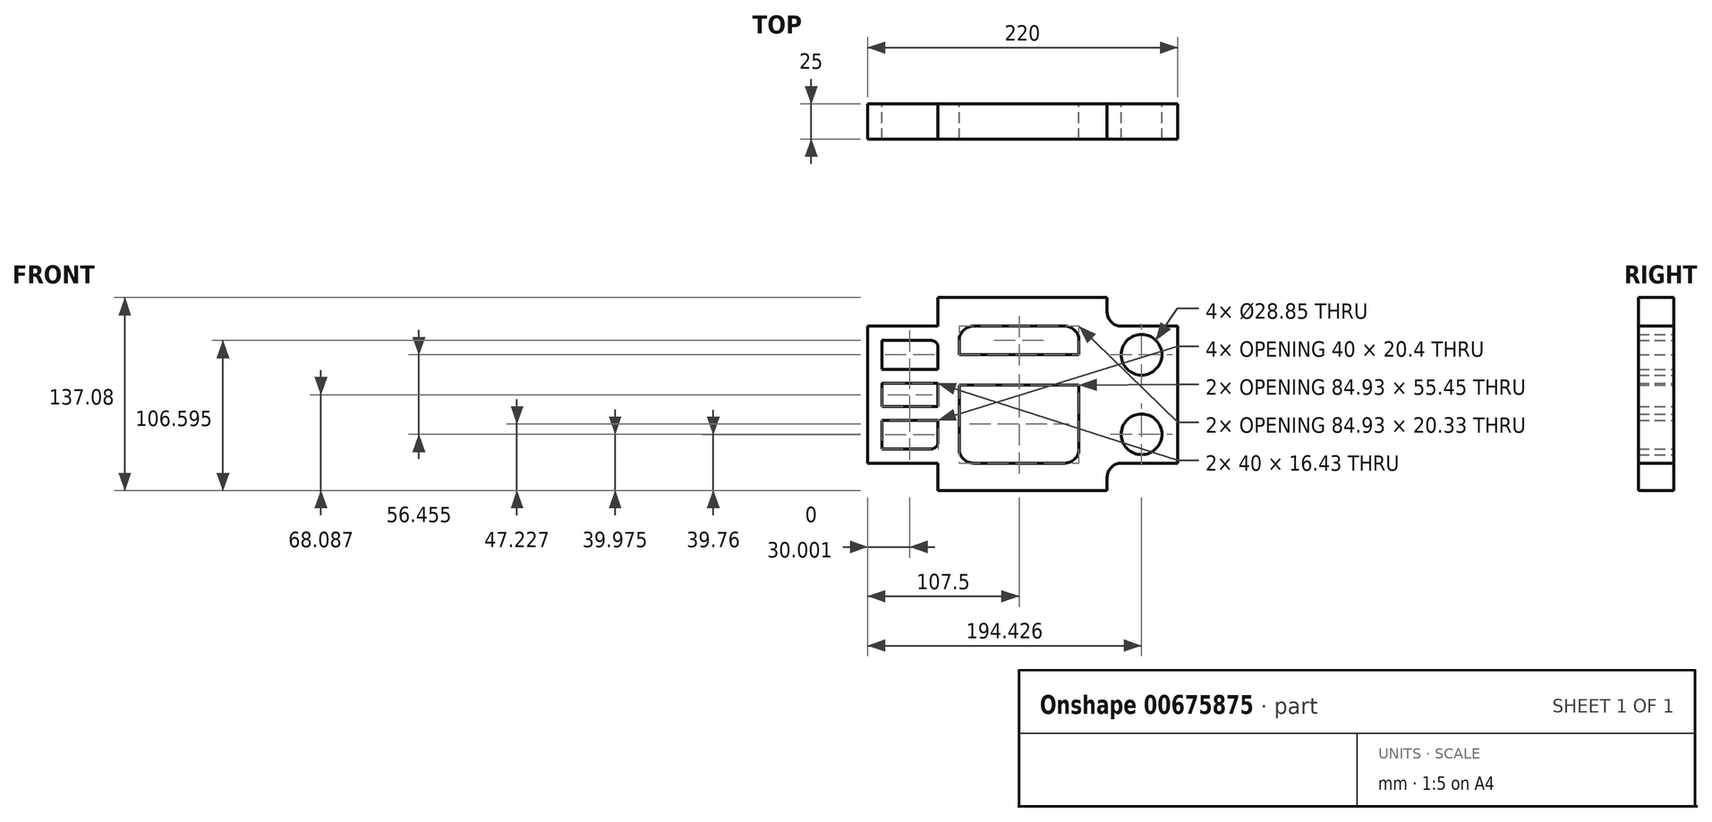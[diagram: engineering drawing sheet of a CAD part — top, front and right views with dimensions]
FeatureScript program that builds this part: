
annotation { "Feature Type Name" : "Feature", "Feature Type Description" : "" }
export const myFeature = defineFeature(function(context is Context, id is Id, definition is map)
    precondition{}
    {
        {
            var Q0;
            Q0=qCreatedBy(makeId("Front.planeOp"),FACE);
            var sketch = newSketch(context, id + "F0", { "sketchPlane" : qUnion([Q0])});
            skLineSegment(sketch, "E0", {"start": v(-52.53, 54.48) * mm, "end": v(-52.53, -42.78) * mm});
            skLineSegment(sketch, "E1", {"start": v(-52.53, -42.78) * mm, "end": v(-2.53, -42.78) * mm});
            skLineSegment(sketch, "E2", {"start": v(-2.53, -42.78) * mm, "end": v(-2.53, -62.28) * mm});
            skLineSegment(sketch, "E3", {"start": v(-2.53, -62.28) * mm, "end": v(117.47, -62.28) * mm});
            skLineSegment(sketch, "E4", {"start": v(117.47, -62.28) * mm, "end": v(117.47, -52.78) * mm});
            skLineSegment(sketch, "E5", {"start": v(127.47, -42.78) * mm, "end": v(167.47, -42.78) * mm});
            skLineSegment(sketch, "E6", {"start": v(167.47, -42.78) * mm, "end": v(167.47, 54.48) * mm});
            skLineSegment(sketch, "E7", {"start": v(167.47, 54.48) * mm, "end": v(127.47, 54.48) * mm});
            skLineSegment(sketch, "E8", {"start": v(117.47, 64.48) * mm, "end": v(117.47, 74.8) * mm});
            skLineSegment(sketch, "E9", {"start": v(117.47, 74.8) * mm, "end": v(-2.53, 74.8) * mm});
            skLineSegment(sketch, "E10", {"start": v(-2.53, 74.8) * mm, "end": v(-2.53, 54.48) * mm});
            skLineSegment(sketch, "E11", {"start": v(-2.53, 54.48) * mm, "end": v(-52.53, 54.48) * mm});
            skLineSegment(sketch, "E12", {"start": v(-2.53, 39.33) * mm, "end": v(-2.53, 23.94) * mm});
            skLineSegment(sketch, "E13", {"start": v(-42.53, -32.72) * mm, "end": v(-42.53, -12.32) * mm});
            skLineSegment(sketch, "E14", {"start": v(-42.53, -32.72) * mm, "end": v(-7.53, -32.72) * mm});
            skLineSegment(sketch, "E15", {"start": v(-42.53, 44.33) * mm, "end": v(-7.53, 44.33) * mm});
            skLineSegment(sketch, "E16", {"start": v(-42.53, -12.32) * mm, "end": v(-2.53, -12.32) * mm});
            skLineSegment(sketch, "E17", {"start": v(-42.53, 44.33) * mm, "end": v(-42.53, 23.94) * mm});
            skLineSegment(sketch, "E18", {"start": v(-42.53, 23.94) * mm, "end": v(-2.53, 23.94) * mm});
            skLineSegment(sketch, "E19", {"start": v(-42.53, 14.02) * mm, "end": v(-2.53, 14.02) * mm});
            skLineSegment(sketch, "E20", {"start": v(-42.53, -2.4) * mm, "end": v(-2.53, -2.4) * mm});
            skLineSegment(sketch, "E21.trimOffspring", {"start": v(-2.53, 14.02) * mm, "end": v(-2.53, -2.4) * mm});
            skLineSegment(sketch, "E22.trimOffspring", {"start": v(-42.53, 23.94) * mm, "end": v(-42.53, 44.33) * mm});
            skLineSegment(sketch, "E23.trimOffspring", {"start": v(-42.53, -2.4) * mm, "end": v(-42.53, 14.02) * mm});
            skLineSegment(sketch, "E24.trimOffspring", {"start": v(-2.53, -12.32) * mm, "end": v(-2.53, -27.72) * mm});
            skPoint(sketch, "E25.visualSharp", {"position": v(-2.53, 44.33) * mm});
            skArc(sketch, "E25.filletArc", {"start": v(-2.53, 39.33) * mm, "mid": v(-4, 42.87) * mm, "end": v(-7.53, 44.33) * mm});
            skPoint(sketch, "E26.visualSharp", {"position": v(-2.53, -32.72) * mm});
            skArc(sketch, "E26.filletArc", {"start": v(-7.53, -32.72) * mm, "mid": v(-4, -31.25) * mm, "end": v(-2.53, -27.72) * mm});
            skLineSegment(sketch, "E27", {"start": v(22.5, -42.78) * mm, "end": v(87.44, -42.78) * mm});
            skLineSegment(sketch, "E28", {"start": v(22.5, 54.48) * mm, "end": v(87.44, 54.48) * mm});
            skLineSegment(sketch, "E29", {"start": v(12.5, 34.15) * mm, "end": v(12.5, 44.48) * mm});
            skLineSegment(sketch, "E30", {"start": v(97.44, 34.15) * mm, "end": v(97.44, 44.48) * mm});
            skLineSegment(sketch, "E31", {"start": v(97.44, 34.15) * mm, "end": v(12.5, 34.15) * mm});
            skPoint(sketch, "E32.start.orphan", {"position": v(-2.53, 29.15) * mm});
            skPoint(sketch, "E33.start.orphan", {"position": v(57.47, 54.48) * mm});
            skLineSegment(sketch, "E34", {"start": v(52.47, 12.67) * mm, "end": v(12.5, 12.67) * mm});
            skLineSegment(sketch, "E35", {"start": v(12.5, 12.67) * mm, "end": v(97.44, 12.67) * mm});
            skLineSegment(sketch, "E36", {"start": v(97.44, -32.78) * mm, "end": v(97.44, 12.67) * mm});
            skLineSegment(sketch, "E37", {"start": v(12.5, 12.67) * mm, "end": v(12.5, -32.78) * mm});
            skPoint(sketch, "E38.start.orphan", {"position": v(57.47, -42.78) * mm});
            skArc(sketch, "E39.filletArc", {"start": v(12.5, -32.78) * mm, "mid": v(15.43, -39.85) * mm, "end": v(22.5, -42.78) * mm});
            skArc(sketch, "E40.filletArc", {"start": v(87.44, -42.78) * mm, "mid": v(94.5, -39.85) * mm, "end": v(97.44, -32.78) * mm});
            skArc(sketch, "E41.filletArc", {"start": v(97.44, 44.48) * mm, "mid": v(94.5, 51.55) * mm, "end": v(87.44, 54.48) * mm});
            skArc(sketch, "E42.filletArc", {"start": v(22.5, 54.48) * mm, "mid": v(15.43, 51.55) * mm, "end": v(12.5, 44.48) * mm});
            skArc(sketch, "E43.filletArc", {"start": v(117.47, 64.48) * mm, "mid": v(120.4, 57.4) * mm, "end": v(127.47, 54.48) * mm});
            skArc(sketch, "E44.filletArc", {"start": v(127.47, -42.78) * mm, "mid": v(120.4, -45.7) * mm, "end": v(117.47, -52.78) * mm});
            skCircle(sketch, "E45", {"center": v(141.9, -22.3) * mm, "radius": 14.43 * mm});
            skCircle(sketch, "E46", {"center": v(141.9, 34.15) * mm, "radius": 14.43 * mm});
            skSolve(sketch);
        }
        {
            var Q0;
            Q0 = qSketchRegion(id + "F0", true);
            extrude(context, id + "F1", {"entities" : qUnion([Q0]), "depth" : 25 * mm, "offsetDistance" : 25 * mm});
        }
    });
